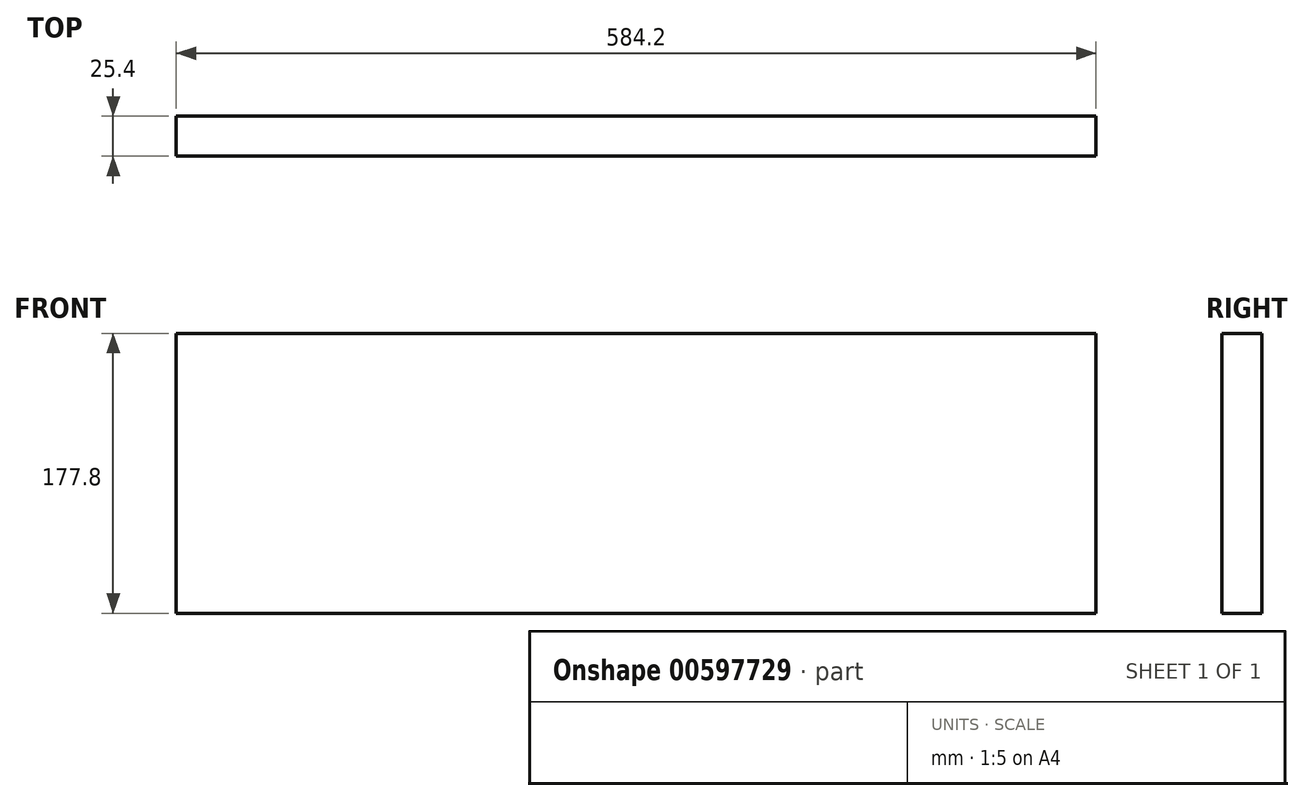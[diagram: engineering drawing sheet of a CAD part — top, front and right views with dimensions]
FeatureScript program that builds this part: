
annotation { "Feature Type Name" : "Feature", "Feature Type Description" : "" }
export const myFeature = defineFeature(function(context is Context, id is Id, definition is map)
    precondition{}
    {
        {
            var Q0;
            Q0=qCreatedBy(makeId("Front.planeOp"),FACE);
            var sketch = newSketch(context, id + "F0", { "sketchPlane" : qUnion([Q0])});
            skLineSegment(sketch, "E0.bottom", {"start": v(-584.2, 177.8) * mm, "end": v(0, 177.8) * mm});
            skLineSegment(sketch, "E0.top", {"start": v(-584.2, 0) * mm, "end": v(0, 0) * mm});
            skLineSegment(sketch, "E0.left", {"start": v(-584.2, 177.8) * mm, "end": v(-584.2, 0) * mm});
            skLineSegment(sketch, "E0.right", {"start": v(0, 177.8) * mm, "end": v(0, 0) * mm});
            skSolve(sketch);
        }
        {
            var Q0;
            Q0 = qSketchRegion(id + "F0", true);
            extrude(context, id + "F1", {"entities" : qUnion([Q0]), "depth" : 25.4 * mm, "offsetDistance" : 25.4 * mm});
        }
    });
